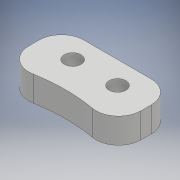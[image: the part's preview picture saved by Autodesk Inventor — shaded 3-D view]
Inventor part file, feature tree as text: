
AUTODESK INVENTOR PART (.ipt)
format: ipt  version: 2018 (Build 220112000, 112)  size: 121,856 bytes
history: native  units: mm
features: extrude x2, sketch x2, other x1, fillet x1
ambient origin geometry x8: Origin, YZ Plane, XZ Plane, XY Plane, X Axis, Y Axis, Z Axis, Center Point
bodies: Body1 (feature_tree)
feature tree (6):
  other  "ソリッド1"
  extrude  "押し出し1"  Depth=20.0mm
  fillet  "フィレット1"  Radius=11.0mm
  extrude  "押し出し2"  Depth=30.0mm
  sketch  "スケッチ1"
  sketch  "スケッチ2"
